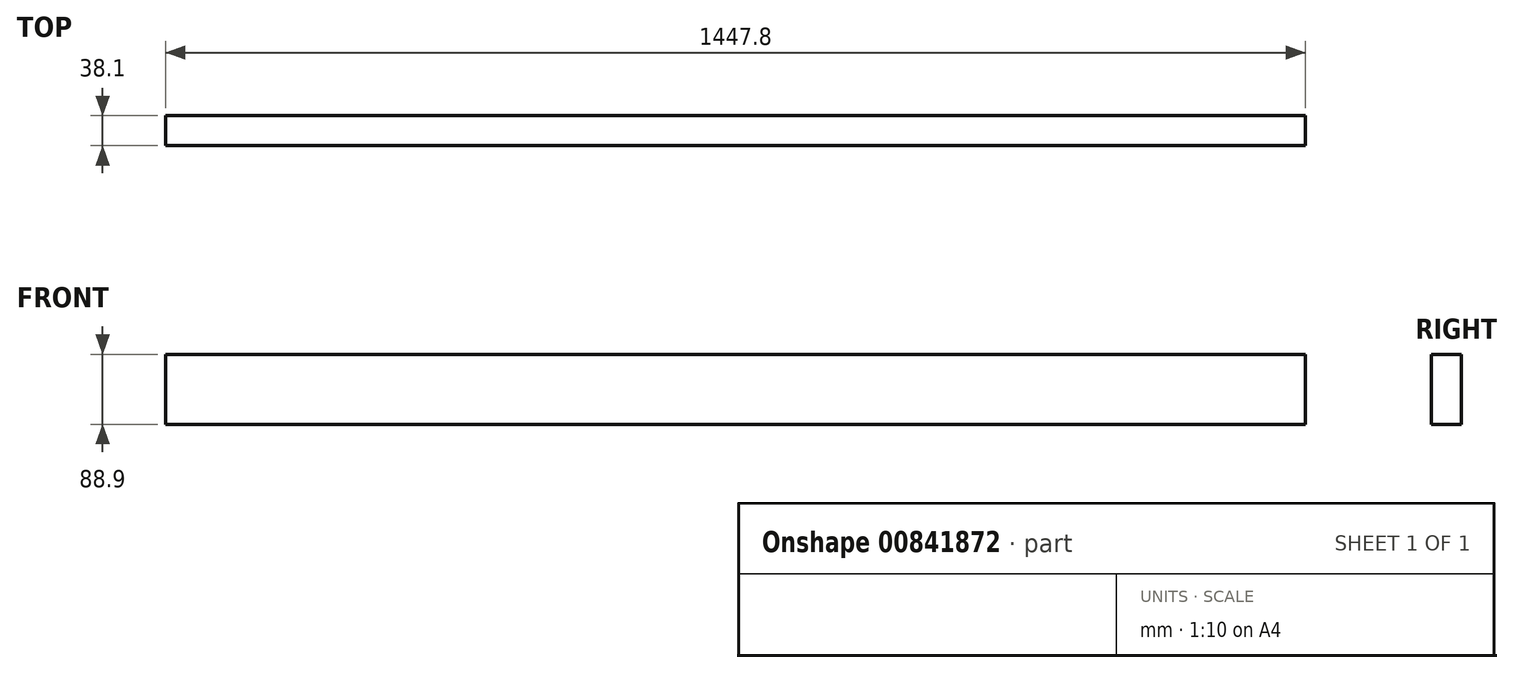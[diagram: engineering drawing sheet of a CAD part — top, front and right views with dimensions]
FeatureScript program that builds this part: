
annotation { "Feature Type Name" : "Feature", "Feature Type Description" : "" }
export const myFeature = defineFeature(function(context is Context, id is Id, definition is map)
    precondition{}
    {
        {
            var Q0;
            Q0=qCreatedBy(makeId("Right.planeOp"),FACE);
            var sketch = newSketch(context, id + "F0", { "sketchPlane" : qUnion([Q0])});
            skLineSegment(sketch, "E0.bottom", {"start": v(19.05, 44.45) * mm, "end": v(-19.05, 44.45) * mm});
            skLineSegment(sketch, "E0.top", {"start": v(19.05, -44.45) * mm, "end": v(-19.05, -44.45) * mm});
            skLineSegment(sketch, "E0.left", {"start": v(19.05, 44.45) * mm, "end": v(19.05, -44.45) * mm});
            skLineSegment(sketch, "E0.right", {"start": v(-19.05, 44.45) * mm, "end": v(-19.05, -44.45) * mm});
            skPoint(sketch, "E0.middle", {"position": v(0, 0) * mm});
            skSolve(sketch);
        }
        {
            var Q0;
            Q0 = qSketchRegion(id + "F0", true);
            extrude(context, id + "F1", {"entities" : qUnion([Q0]), "depth" : 1447.8 * mm, "offsetDistance" : 25.4 * mm});
        }
    });
